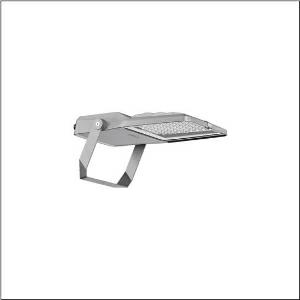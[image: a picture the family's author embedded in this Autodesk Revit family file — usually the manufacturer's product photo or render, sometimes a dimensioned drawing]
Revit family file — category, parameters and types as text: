
# Revit family: floodlight_fl_21_iq_mini___pl33t_5xa7772d2f1a_a564
name_source: partatom
category: Lighting Fixtures
units: mm (PartAtom-declared; Revit-internal decimal feet)

## family parameters
Cut with Voids When Loaded = No
Host = Face
Light Source = No
Part Type = Normal
Room Calculation Point = No
Round Connector Dimension = Use Diameter
Shared = No

## types (1)
- --- (1 x LED, 17620 lm, 143 W, 3000K)
    Apparent Load = 143 VA
    CIE Flux Codes = 26 75 99 100 100
    Color Rendering = 70
    Color Temperature = 3000K
    Default Elevation = 1800 mm
    Description = Floodlight FL 21 iQ mini, floodlight, primary light control with lens, of PMMA, primary optical cover: protective disc, of toughened safety glass, transparent, light distribution: PL33T, light emission: direct distribution, installation type: surface-mounted, LED, High Power LED, rated luminous flux: 17.620lm, luminous efficacy: 123lm/W, light colour: 730, colour temperature: 3000K, control gear: iQ Street-Remote/DALI, control: Street-Remote, Auto-Match, Temp-Guard, Night-Set, Smart-Wire, Desk-Remote (wireless, voltage-free reading and setting of iQ features in the workshop via application-optimized NFC function/RFID function), optimised constant luminous flux control (CLO 2.0), with terminal, 6-pole, mains connection: 220..240V, AC, 50/60Hz, start of lifetime: 143W, end of service life: 152W, reduction: 61W, luminaire housing, of diecast aluminium, powder-coated, Siteco® metallic grey (DB 702S), corrosivity category C5 mid according to DIN EN ISO 12944, suitable for swimming pools, chlorine-resistant, sealing non-destructively replaceable, mounting bracket, of steel, galvanised, powder-coated, Siteco® metallic grey (DB 702S), protection rating (complete): IP66, insulation class (complete): insulation class II (safety insulation), certification: CE, ENEC, VDE, protection symbol: D, impact resistance: IK08, permissible operating ambient temperature: -40..+40°C, permissible operating ambient temperature for outdoor applications: -40..+50°C, standard: DIN EN 12944, LABS conformity tested according to VDMA 24364:2018-05, packaging unit: 1 piece

Light Distribution: PL33T
    Height = 70 mm
    Lamp = 1 x LED
    Lamp Light Flux = 17620 lm
    Lamp Power = 143 W
    Lamp count = 1
    Length = 485 mm
    Luminous efficacy = 123 lm/W
    Manufacturer = Siteco
    ModVariant = No
    Model = 5XA7772D2F1A
    Number of Poles = 1
    OnlyDefault = Yes
    Power Factor = 1
    Product Name = Floodlight FL 21 iQ mini | PL33T
    Product group = floodlight | pylon annexe
    ProductGroupID = 6200
    Protection Class = Protection class II
    Protection Degree = IP 66
    RLX_Detail_Level = 1
    RLX_Emergency_Light_Flux = 0 lm
    RLX_Emergency_Type = 0
    RLX_Emergency_Type_DB = No
    RlxData = <blob elided: 96389 chars, md5=25e2f4d2>
    Socket = socket
    Standby Power = 0 W
    System Light Flux = 17620 lm
    System Power = 143 W
    Type Comments = factory setting: luminous flux: 100 % | dim-lin: 254 | 730 mA
    Type Image = l_1006845.jpg
    URL = http://relux.com
    VarID = @adj_149008
    Voltage = 0 V
    Weight = 0.00 kg
    Width = 337 mm

## geometry (parser evidence)
native form markers: Blend x4, Sweep x11
no freeform markers — native parametric forms only
